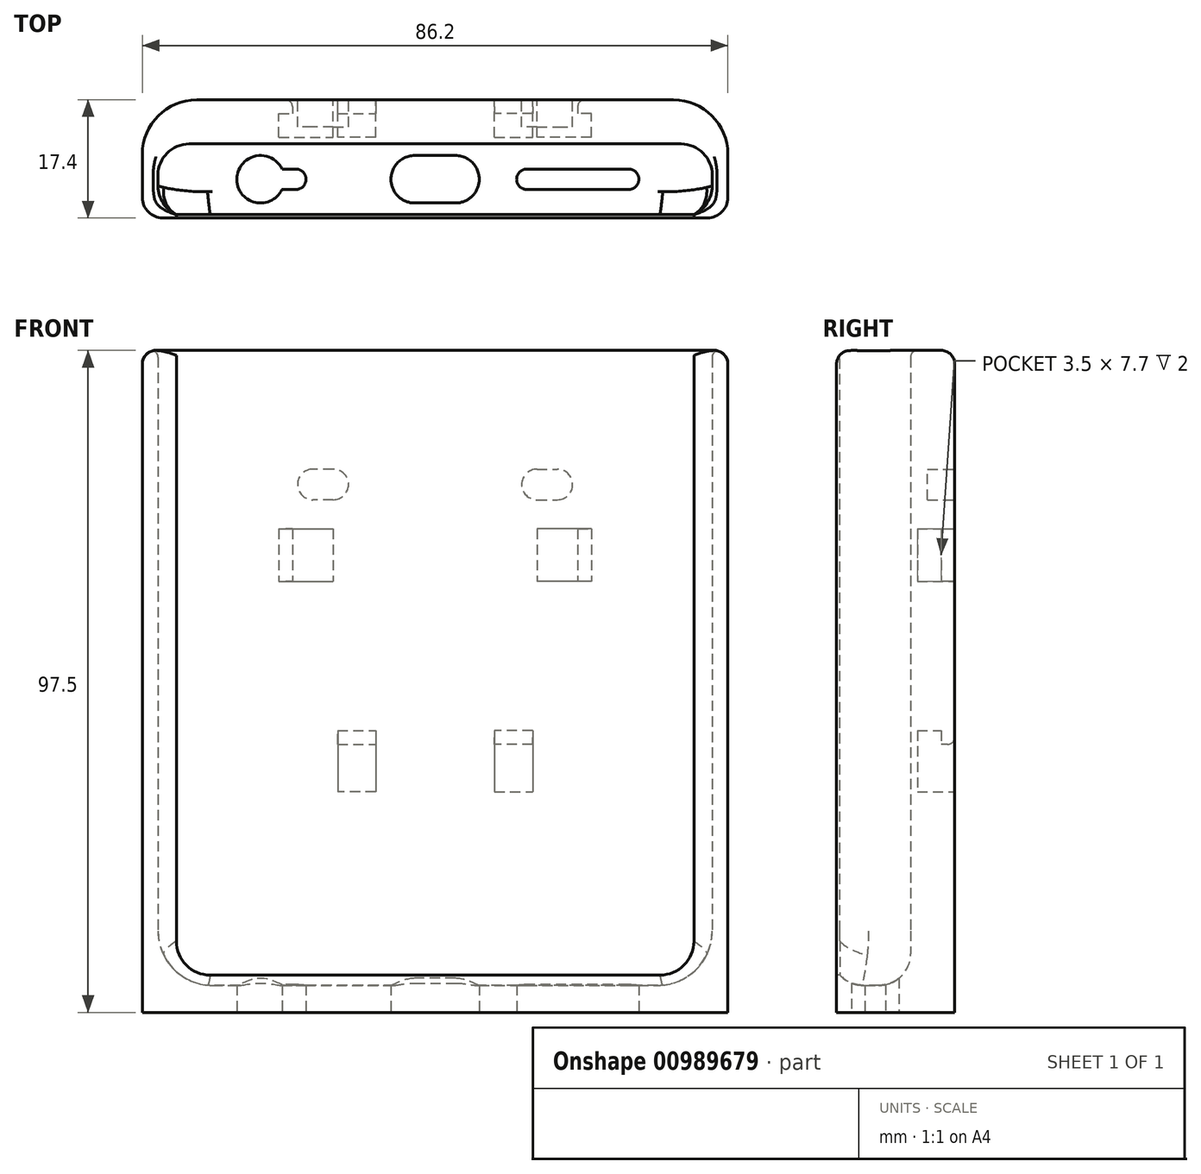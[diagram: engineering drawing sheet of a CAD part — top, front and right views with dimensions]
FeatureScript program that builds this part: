
annotation { "Feature Type Name" : "Feature", "Feature Type Description" : "" }
export const myFeature = defineFeature(function(context is Context, id is Id, definition is map)
    precondition{}
    {
        {
            var Q0;
            Q0=qCreatedBy(makeId("Front.planeOp"),FACE);
            var sketch = newSketch(context, id + "F0", { "sketchPlane" : qUnion([Q0])});
            skLineSegment(sketch, "E0", {"start": v(0, -32.88) * mm, "end": v(0, 44.67) * mm, "construction": true});
            skLineSegment(sketch, "E1.bottom", {"start": v(-23, 39.76) * mm, "end": v(-15, 39.76) * mm});
            skLineSegment(sketch, "E1.top", {"start": v(-23, 32.06) * mm, "end": v(-15, 32.06) * mm});
            skLineSegment(sketch, "E1.left", {"start": v(-23, 39.76) * mm, "end": v(-23, 32.06) * mm});
            skLineSegment(sketch, "E1.right", {"start": v(-15, 39.76) * mm, "end": v(-15, 32.06) * mm});
            skLineSegment(sketch, "E2.bottom", {"start": v(-8.75, 10.06) * mm, "end": v(-14.35, 10.06) * mm});
            skLineSegment(sketch, "E2.top", {"start": v(-8.75, 1.06) * mm, "end": v(-14.35, 1.06) * mm});
            skLineSegment(sketch, "E2.left", {"start": v(-8.75, 10.06) * mm, "end": v(-8.75, 1.06) * mm});
            skLineSegment(sketch, "E2.right", {"start": v(-14.35, 10.06) * mm, "end": v(-14.35, 1.06) * mm});
            skLineSegment(sketch, "E3.MirrorCS", {"start": v(15, 39.76) * mm, "end": v(15, 32.06) * mm});
            skLineSegment(sketch, "E4.MirrorCS", {"start": v(23, 32.06) * mm, "end": v(15, 32.06) * mm});
            skLineSegment(sketch, "E5.MirrorCS", {"start": v(23, 39.76) * mm, "end": v(23, 32.06) * mm});
            skLineSegment(sketch, "E6.MirrorCS", {"start": v(23, 39.76) * mm, "end": v(15, 39.76) * mm});
            skLineSegment(sketch, "E7.MirrorCS", {"start": v(8.75, 10.06) * mm, "end": v(14.35, 10.06) * mm});
            skLineSegment(sketch, "E8.MirrorCS", {"start": v(8.75, 10.06) * mm, "end": v(8.75, 1.06) * mm});
            skLineSegment(sketch, "E9.MirrorCS", {"start": v(8.75, 1.06) * mm, "end": v(14.35, 1.06) * mm});
            skLineSegment(sketch, "E10.MirrorCS", {"start": v(14.35, 10.06) * mm, "end": v(14.35, 1.06) * mm});
            skSolve(sketch);
        }
        {
            var Q0;
            Q0=qCreatedBy(makeId("Front.planeOp"),FACE);
            var sketch = newSketch(context, id + "F1", { "sketchPlane" : qUnion([Q0])});
            skLineSegment(sketch, "E11", {"start": v(0, -37.74) * mm, "end": v(0, 51.46) * mm, "construction": true});
            skLineSegment(sketch, "E12.bottom", {"start": v(0, 66.06) * mm, "end": v(-40.6, 66.06) * mm});
            skLineSegment(sketch, "E12.top", {"start": v(0, -28.94) * mm, "end": v(-32.6, -28.94) * mm});
            skLineSegment(sketch, "E12.left", {"start": v(0, 66.06) * mm, "end": v(0, -28.94) * mm});
            skLineSegment(sketch, "E12.right", {"start": v(-40.6, 66.06) * mm, "end": v(-40.6, -20.94) * mm});
            skPoint(sketch, "E13.visualSharp", {"position": v(-40.6, -28.94) * mm});
            skArc(sketch, "E13.filletArc", {"start": v(-40.6, -20.94) * mm, "mid": v(-38.26, -26.6) * mm, "end": v(-32.6, -28.94) * mm});
            skSolve(sketch);
        }
        {
            var Q0;
            Q0=qCreatedBy(makeId("Front.planeOp"),FACE);
            var sketch = newSketch(context, id + "F2", { "sketchPlane" : qUnion([Q0])});
            skLineSegment(sketch, "E14.bottom", {"start": v(0, 66.06) * mm, "end": v(-43.1, 66.06) * mm});
            skLineSegment(sketch, "E14.top", {"start": v(0, -31.44) * mm, "end": v(-43.1, -31.44) * mm});
            skLineSegment(sketch, "E14.right", {"start": v(-43.1, 66.06) * mm, "end": v(-43.1, -31.44) * mm});
            skPoint(sketch, "E15.visualSharp", {"position": v(-43.1, -31.44) * mm});
            skLineSegment(sketch, "E15.filletArc", {"start": v(-43.1, -31.44) * mm, "end": v(-43.1, -31.44) * mm});
            skLineSegment(sketch, "E16.MirrorCS", {"start": v(0, 66.06) * mm, "end": v(43.1, 66.06) * mm});
            skLineSegment(sketch, "E17.MirrorCS", {"start": v(43.1, 66.06) * mm, "end": v(43.1, -31.44) * mm});
            skLineSegment(sketch, "E18.MirrorCS", {"start": v(43.1, -31.44) * mm, "end": v(43.1, -31.44) * mm});
            skLineSegment(sketch, "E19.MirrorCS", {"start": v(0, -31.44) * mm, "end": v(43.1, -31.44) * mm});
            skSolve(sketch);
        }
        {
            var Q0;
            Q0=qSketchRegion(id+"F2",true);
            extrude(context, id + "F3", {"entities" : qUnion([Q0]), "depth" : 17.4 * mm, "offsetDistance" : 25 * mm});
        }
        {
            var Q0;
            Q0=qSketchRegion(id+"F0",true);
            extrude(context, id + "F4", {"entities" : qUnion([Q0]), "operationType" : NewBodyOperationType.REMOVE, "depth" : 5.5 * mm, "offsetDistance" : 25 * mm});
        }
        {
            var Q0;
            Q0=qCreatedBy(makeId("Front.planeOp"),FACE);
            cPlane(context, id + "F5", {"entities" : qUnion([Q0]), "cplaneType" : CPlaneType.OFFSET, "offset" : 6.5 * mm, "width" : 150 * mm, "height" : 150 * mm});
        }
        {
            var Q0;
            Q0=qCreatedBy(id+"F5.planeOp",FACE);
            var sketch = newSketch(context, id + "F6", { "sketchPlane" : qUnion([Q0])});
            skLineSegment(sketch, "E20", {"start": v(0, -47.03) * mm, "end": v(0, 63.52) * mm, "construction": true});
            skLineSegment(sketch, "E21.right", {"start": v(0, 66.06) * mm, "end": v(0, 51.73) * mm, "construction": true});
            skLineSegment(sketch, "E22.bottom", {"start": v(-40.8, 66.06) * mm, "end": v(0, 66.06) * mm});
            skLineSegment(sketch, "E22.top", {"start": v(-32.8, -27.44) * mm, "end": v(0, -27.44) * mm});
            skLineSegment(sketch, "E22.left", {"start": v(-40.8, 66.06) * mm, "end": v(-40.8, -19.44) * mm});
            skLineSegment(sketch, "E22.right", {"start": v(0, 66.06) * mm, "end": v(0, -27.44) * mm});
            skPoint(sketch, "E23.visualSharp", {"position": v(-40.8, -27.44) * mm});
            skArc(sketch, "E23.filletArc", {"start": v(-40.8, -19.44) * mm, "mid": v(-38.46, -25.1) * mm, "end": v(-32.8, -27.44) * mm});
            skLineSegment(sketch, "E24.MirrorCS", {"start": v(32.8, -27.44) * mm, "end": v(0, -27.44) * mm});
            skArc(sketch, "E25.MirrorCS", {"start": v(40.8, -19.44) * mm, "mid": v(38.46, -25.1) * mm, "end": v(32.8, -27.44) * mm});
            skLineSegment(sketch, "E26.MirrorCS", {"start": v(40.8, 66.06) * mm, "end": v(40.8, -19.44) * mm});
            skLineSegment(sketch, "E27.MirrorCS", {"start": v(40.8, 66.06) * mm, "end": v(0, 66.06) * mm});
            skSolve(sketch);
        }
        {
            var Q0;
            Q0=qSketchRegion(id+"F6",true);
            extrude(context, id + "F7", {"entities" : qUnion([Q0]), "operationType" : NewBodyOperationType.REMOVE, "depth" : 10.4 * mm, "offsetDistance" : 25 * mm});
        }
        {
            var Q0;
            Q0=makeQuery(id+"F3.opExtrude","CAP_FACE",FACE,{"disambiguationData":[OSD([sQuery(id+"F2.wireOp",EDGE,"E14.bottom"),sQuery(id+"F2.wireOp",EDGE,"E14.top"),sQuery(id+"F2.wireOp",EDGE,"E14.right"),sQuery(id+"F2.wireOp",EDGE,"E15.filletArc"),sQuery(id+"F2.wireOp",EDGE,"E16.MirrorCS"),sQuery(id+"F2.wireOp",EDGE,"E17.MirrorCS"),sQuery(id+"F2.wireOp",EDGE,"E18.MirrorCS"),sQuery(id+"F2.wireOp",EDGE,"E19.MirrorCS")])],"isStart":false});
            var sketch = newSketch(context, id + "F8", { "sketchPlane" : qUnion([Q0])});
            skLineSegment(sketch, "E28", {"start": v(0, 66.06) * mm, "end": v(0, 61.95) * mm, "construction": true});
            skLineSegment(sketch, "E29.bottom", {"start": v(-38.1, 66.06) * mm, "end": v(0, 66.06) * mm});
            skLineSegment(sketch, "E29.top", {"start": v(-33.1, -25.94) * mm, "end": v(0, -25.94) * mm});
            skLineSegment(sketch, "E29.left", {"start": v(-38.1, 66.06) * mm, "end": v(-38.1, -20.94) * mm});
            skPoint(sketch, "E30.visualSharp", {"position": v(-38.1, -25.94) * mm});
            skArc(sketch, "E30.filletArc", {"start": v(-38.1, -20.94) * mm, "mid": v(-36.64, -24.48) * mm, "end": v(-33.1, -25.94) * mm});
            skLineSegment(sketch, "E31.trimOffspring", {"start": v(0, -25.94) * mm, "end": v(0, -47.05) * mm, "construction": true});
            skLineSegment(sketch, "E32.MirrorCS", {"start": v(33.1, -25.94) * mm, "end": v(0, -25.94) * mm});
            skArc(sketch, "E33.MirrorCS", {"start": v(38.1, -20.94) * mm, "mid": v(36.64, -24.48) * mm, "end": v(33.1, -25.94) * mm});
            skLineSegment(sketch, "E34.MirrorCS", {"start": v(38.1, 66.06) * mm, "end": v(38.1, -20.94) * mm});
            skLineSegment(sketch, "E35.MirrorCS", {"start": v(38.1, 66.06) * mm, "end": v(0, 66.06) * mm});
            skSolve(sketch);
        }
        {
            var Q0;
            Q0=qSketchRegion(id+"F8",true);
            extrude(context, id + "F9", {"entities" : qUnion([Q0]), "operationType" : NewBodyOperationType.REMOVE, "endBound" : BoundingType.UP_TO_NEXT, "oppositeDirection" : true, "depth" : 25 * mm, "offsetDistance" : 25 * mm});
        }
        {
            var Q0;
            Q0=makeQuery(id+"F7.boolean.opBoolean","COPY",EDGE,{"derivedFrom":makeQuery(id+"F7.opExtrude","CAP_EDGE",EDGE,{"disambiguationData":[OSD([sQuery(id+"F6.wireOp",EDGE,"E22.left")])],"isStart":true})});
            fillet(context, id + "F10", {"entities" : qUnion([Q0]), "radius" : 4.6 * mm, "tangentPropagation" : true, "allowEdgeOverflow" : false});
        }
        {
            var Q0;
            Q0=makeQuery(id+"F7.boolean.opBoolean","COPY",EDGE,{"derivedFrom":makeQuery(id+"F7.opExtrude","CAP_EDGE",EDGE,{"disambiguationData":[OSD([sQuery(id+"F6.wireOp",EDGE,"E22.left")])],"isStart":false})});
            fillet(context, id + "F11", {"entities" : qUnion([Q0]), "radius" : 4.6 * mm, "tangentPropagation" : true, "allowEdgeOverflow" : false});
        }
        {
            var Q0;
            Q0=makeQuery(id+"F11.opFillet","BLEND_EDGE",EDGE,{"blendedFrom":[makeQuery(id+"F7.boolean.opBoolean","COPY",EDGE,{"derivedFrom":makeQuery(id+"F7.opExtrude","CAP_EDGE",EDGE,{"disambiguationData":[OSD([sQuery(id+"F6.wireOp",EDGE,"E26.MirrorCS")])],"isStart":false})}),makeQuery(id+"F3.opExtrude","SWEPT_FACE",FACE,{"disambiguationData":[OSD([sQuery(id+"F2.wireOp",EDGE,"E14.bottom"),sQuery(id+"F2.wireOp",EDGE,"E16.MirrorCS")])]})],"blendedInto":[makeQuery(id+"F3.opExtrude","SWEPT_FACE",FACE,{"disambiguationData":[OSD([sQuery(id+"F2.wireOp",EDGE,"E14.bottom"),sQuery(id+"F2.wireOp",EDGE,"E16.MirrorCS")])]})]});
            var Q1;
            {var subQ0=sQuery(id+"F6.wireOp",EDGE,"E27.MirrorCS");var subQ1=sQuery(id+"F6.wireOp",EDGE,"E26.MirrorCS");var subQ2=sQuery(id+"F6.wireOp",EDGE,"E22.bottom");Q1=makeQuery(id+"F9.boolean.opBoolean","SPLIT",EDGE,{"disambiguationData":[TD([makeQuery(id+"F7.boolean.opBoolean","COPY",FACE,{"derivedFrom":makeQuery(id+"F7.opExtrude","SWEPT_FACE",FACE,{"disambiguationData":[OSD([subQ1])]})})])],"derivedFrom":makeQuery(id+"F7.boolean.opBoolean","COPY",EDGE,{"derivedFrom":makeQuery(id+"F7.opExtrude","CAP_EDGE",EDGE,{"disambiguationData":[OSD([subQ2,subQ0])],"isStart":false})})});}
            fillet(context, id + "F12", {"entities" : qUnion([Q0, Q1]), "radius" : 1 * mm, "tangentPropagation" : true, "allowEdgeOverflow" : false});
        }
        {
            var Q0;
            Q0=makeQuery(id+"F4.boolean.opBoolean","COPY",FACE,{"derivedFrom":makeQuery(id+"F4.opExtrude","SWEPT_FACE",FACE,{"disambiguationData":[OSD([sQuery(id+"F0.wireOp",EDGE,"E4.MirrorCS")])]})});
            var sketch = newSketch(context, id + "F13", { "sketchPlane" : qUnion([Q0])});
            skLineSegment(sketch, "E36.bottom", {"start": v(23, 0) * mm, "end": v(22, 0) * mm});
            skLineSegment(sketch, "E36.top", {"start": v(23, -2) * mm, "end": v(21, -2) * mm});
            skLineSegment(sketch, "E36.left", {"start": v(23, 0) * mm, "end": v(23, -2) * mm});
            skLineSegment(sketch, "E36.right", {"start": v(21, -1) * mm, "end": v(21, -2) * mm});
            skPoint(sketch, "E37.visualSharp", {"position": v(21, 0) * mm});
            skArc(sketch, "E37.filletArc", {"start": v(22, 0) * mm, "mid": v(21.3, -0.3) * mm, "end": v(21, -1) * mm});
            skSolve(sketch);
        }
        {
            var Q0;
            Q0=qSketchRegion(id+"F13",true);
            extrude(context, id + "F14", {"entities" : qUnion([Q0]), "operationType" : NewBodyOperationType.ADD, "endBound" : BoundingType.UP_TO_NEXT, "depth" : 25 * mm, "offsetDistance" : 25 * mm});
        }
        {
            var Q0;
            Q0=makeQuery(id+"F4.boolean.opBoolean","COPY",FACE,{"derivedFrom":makeQuery(id+"F4.opExtrude","SWEPT_FACE",FACE,{"disambiguationData":[OSD([sQuery(id+"F0.wireOp",EDGE,"E1.top")])]})});
            var sketch = newSketch(context, id + "F15", { "sketchPlane" : qUnion([Q0])});
            skLineSegment(sketch, "E38.bottom", {"start": v(-23, 0) * mm, "end": v(-22, 0) * mm});
            skLineSegment(sketch, "E38.top", {"start": v(-23, -2) * mm, "end": v(-21, -2) * mm});
            skLineSegment(sketch, "E38.left", {"start": v(-23, 0) * mm, "end": v(-23, -2) * mm});
            skLineSegment(sketch, "E38.right", {"start": v(-21, -1) * mm, "end": v(-21, -2) * mm});
            skPoint(sketch, "E39.visualSharp", {"position": v(-21, 0) * mm});
            skArc(sketch, "E39.filletArc", {"start": v(-21, -1) * mm, "mid": v(-21.3, -0.3) * mm, "end": v(-22, 0) * mm});
            skSolve(sketch);
        }
        {
            var Q0;
            Q0=qSketchRegion(id+"F15",true);
            extrude(context, id + "F16", {"entities" : qUnion([Q0]), "operationType" : NewBodyOperationType.ADD, "endBound" : BoundingType.UP_TO_NEXT, "depth" : 25 * mm, "offsetDistance" : 25 * mm});
        }
        {
            var Q0;
            Q0=makeQuery(id+"F4.boolean.opBoolean","COPY",FACE,{"derivedFrom":makeQuery(id+"F4.opExtrude","SWEPT_FACE",FACE,{"disambiguationData":[OSD([sQuery(id+"F0.wireOp",EDGE,"E2.left")])]})});
            var sketch = newSketch(context, id + "F17", { "sketchPlane" : qUnion([Q0])});
            skLineSegment(sketch, "E40.bottom", {"start": v(0, 10.06) * mm, "end": v(2, 10.06) * mm});
            skLineSegment(sketch, "E40.top", {"start": v(1, 8.06) * mm, "end": v(2, 8.06) * mm});
            skLineSegment(sketch, "E40.left", {"start": v(0, 10.06) * mm, "end": v(0, 9.06) * mm});
            skLineSegment(sketch, "E40.right", {"start": v(2, 10.06) * mm, "end": v(2, 8.06) * mm});
            skPoint(sketch, "E41.visualSharp", {"position": v(0, 8.06) * mm});
            skArc(sketch, "E41.filletArc", {"start": v(0, 9.06) * mm, "mid": v(0.3, 8.35) * mm, "end": v(1, 8.06) * mm});
            skSolve(sketch);
        }
        {
            var Q0;
            Q0=qSketchRegion(id+"F17",true);
            extrude(context, id + "F18", {"entities" : qUnion([Q0]), "operationType" : NewBodyOperationType.ADD, "endBound" : BoundingType.UP_TO_NEXT, "depth" : 25 * mm, "offsetDistance" : 25 * mm});
        }
        {
            var Q0;
            Q0=makeQuery(id+"F4.boolean.opBoolean","COPY",FACE,{"derivedFrom":makeQuery(id+"F4.opExtrude","SWEPT_FACE",FACE,{"disambiguationData":[OSD([sQuery(id+"F0.wireOp",EDGE,"E8.MirrorCS")])]})});
            var sketch = newSketch(context, id + "F19", { "sketchPlane" : qUnion([Q0])});
            skLineSegment(sketch, "E42.bottom", {"start": v(0, 10.06) * mm, "end": v(-2, 10.06) * mm});
            skLineSegment(sketch, "E42.top", {"start": v(-1, 8.06) * mm, "end": v(-2, 8.06) * mm});
            skLineSegment(sketch, "E42.left", {"start": v(0, 10.06) * mm, "end": v(0, 9.06) * mm});
            skLineSegment(sketch, "E42.right", {"start": v(-2, 10.06) * mm, "end": v(-2, 8.06) * mm});
            skPoint(sketch, "E43.visualSharp", {"position": v(0, 8.06) * mm});
            skArc(sketch, "E43.filletArc", {"start": v(-1, 8.06) * mm, "mid": v(-0.3, 8.35) * mm, "end": v(0, 9.06) * mm});
            skSolve(sketch);
        }
        {
            var Q0;
            Q0=qSketchRegion(id+"F19",true);
            extrude(context, id + "F20", {"entities" : qUnion([Q0]), "operationType" : NewBodyOperationType.ADD, "endBound" : BoundingType.UP_TO_NEXT, "depth" : 25 * mm, "offsetDistance" : 25 * mm});
        }
        {
            var Q0;
            Q0=makeQuery(id+"F3.opExtrude","SWEPT_FACE",FACE,{"disambiguationData":[OSD([sQuery(id+"F2.wireOp",EDGE,"E14.top"),sQuery(id+"F2.wireOp",EDGE,"E19.MirrorCS")])]});
            var sketch = newSketch(context, id + "F21", { "sketchPlane" : qUnion([Q0])});
            skLineSegment(sketch, "E44", {"start": v(-40.57, 11.7) * mm, "end": v(-17, 11.7) * mm, "construction": true});
            skLineSegment(sketch, "E45", {"start": v(0, 24.83) * mm, "end": v(0, 15.2) * mm, "construction": true});
            skLineSegment(sketch, "E46.bottom", {"start": v(-3, 15.2) * mm, "end": v(0, 15.2) * mm});
            skLineSegment(sketch, "E46.left", {"start": v(-6.5, 11.7) * mm, "end": v(-6.5, 11.7) * mm});
            skLineSegment(sketch, "E47.trimOffspring", {"start": v(0, 8.91) * mm, "end": v(0, -15.6) * mm, "construction": true});
            skPoint(sketch, "E48.visualSharp", {"position": v(-6.5, 15.2) * mm});
            skArc(sketch, "E48.filletArc", {"start": v(-3, 15.2) * mm, "mid": v(-5.47, 14.17) * mm, "end": v(-6.5, 11.7) * mm});
            skArc(sketch, "E49.MirrorCS", {"start": v(-3, 8.2) * mm, "mid": v(-5.47, 9.23) * mm, "end": v(-6.5, 11.7) * mm});
            skLineSegment(sketch, "E50.MirrorCS", {"start": v(-3, 8.2) * mm, "end": v(0, 8.2) * mm});
            skLineSegment(sketch, "E51.MirrorCS", {"start": v(3, 15.2) * mm, "end": v(0, 15.2) * mm});
            skArc(sketch, "E52.MirrorCS", {"start": v(3, 15.2) * mm, "mid": v(5.47, 14.17) * mm, "end": v(6.5, 11.7) * mm});
            skArc(sketch, "E53.MirrorCS", {"start": v(3, 8.2) * mm, "mid": v(5.47, 9.23) * mm, "end": v(6.5, 11.7) * mm});
            skLineSegment(sketch, "E54.MirrorCS", {"start": v(3, 8.2) * mm, "end": v(0, 8.2) * mm});
            skLineSegment(sketch, "E55.trimOffspring", {"start": v(-17, 11.7) * mm, "end": v(38.86, 11.7) * mm, "construction": true});
            skArc(sketch, "E56.0.startCap", {"start": v(13.5, 10.2) * mm, "mid": v(12, 11.7) * mm, "end": v(13.5, 13.2) * mm});
            skArc(sketch, "E56.0.endCap", {"start": v(28.5, 13.2) * mm, "mid": v(30, 11.7) * mm, "end": v(28.5, 10.2) * mm});
            skLineSegment(sketch, "E56.0.left", {"start": v(13.5, 13.2) * mm, "end": v(28.5, 13.2) * mm});
            skLineSegment(sketch, "E56.0.right", {"start": v(13.5, 10.2) * mm, "end": v(28.5, 10.2) * mm});
            skArc(sketch, "E57.0.endCap", {"start": v(-20.5, 13.2) * mm, "mid": v(-19, 11.7) * mm, "end": v(-20.5, 10.2) * mm});
            skLineSegment(sketch, "E57.0.left", {"start": v(-22.54, 13.2) * mm, "end": v(-20.5, 13.2) * mm});
            skLineSegment(sketch, "E57.0.right", {"start": v(-22.54, 10.2) * mm, "end": v(-20.5, 10.2) * mm});
            skArc(sketch, "E58", {"start": v(-22.54, 13.2) * mm, "mid": v(-29.2, 11.7) * mm, "end": v(-22.54, 10.2) * mm});
            skSolve(sketch);
        }
        {
            var Q0;
            Q0=qSketchRegion(id+"F21",true);
            extrude(context, id + "F22", {"entities" : qUnion([Q0]), "operationType" : NewBodyOperationType.REMOVE, "endBound" : BoundingType.UP_TO_NEXT, "oppositeDirection" : true, "depth" : 25 * mm, "offsetDistance" : 25 * mm});
        }
        {
            var Q0;
            Q0=makeQuery(id+"F3.opExtrude","CAP_EDGE",EDGE,{"disambiguationData":[OSD([sQuery(id+"F2.wireOp",EDGE,"E14.right")])],"isStart":true});
            var Q1;
            Q1=makeQuery(id+"F3.opExtrude","CAP_EDGE",EDGE,{"disambiguationData":[OSD([sQuery(id+"F2.wireOp",EDGE,"E17.MirrorCS")])],"isStart":true});
            fillet(context, id + "F23", {"entities" : qUnion([Q0, Q1]), "radius" : 8 * mm, "tangentPropagation" : true, "allowEdgeOverflow" : false});
        }
        {
            var Q0;
            Q0=makeQuery(id+"F3.opExtrude","CAP_EDGE",EDGE,{"disambiguationData":[OSD([sQuery(id+"F2.wireOp",EDGE,"E14.right")])],"isStart":false});
            var Q1;
            Q1=makeQuery(id+"F3.opExtrude","CAP_EDGE",EDGE,{"disambiguationData":[OSD([sQuery(id+"F2.wireOp",EDGE,"E17.MirrorCS")])],"isStart":false});
            fillet(context, id + "F24", {"entities" : qUnion([Q0, Q1]), "radius" : 3 * mm, "tangentPropagation" : true, "allowEdgeOverflow" : false});
        }
        {
            var Q0;
            Q0=makeQuery(id+"F24.opFillet","BLEND_EDGE",EDGE,{"blendedFrom":[makeQuery(id+"F3.opExtrude","CAP_EDGE",EDGE,{"disambiguationData":[OSD([sQuery(id+"F2.wireOp",EDGE,"E14.right")])],"isStart":false}),makeQuery(id+"F3.opExtrude","SWEPT_FACE",FACE,{"disambiguationData":[OSD([sQuery(id+"F2.wireOp",EDGE,"E14.bottom"),sQuery(id+"F2.wireOp",EDGE,"E16.MirrorCS")])]})],"blendedInto":[makeQuery(id+"F3.opExtrude","SWEPT_FACE",FACE,{"disambiguationData":[OSD([sQuery(id+"F2.wireOp",EDGE,"E14.bottom"),sQuery(id+"F2.wireOp",EDGE,"E16.MirrorCS")])]})]});
            fillet(context, id + "F25", {"entities" : qUnion([Q0]), "radius" : 2 * mm, "tangentPropagation" : true, "allowEdgeOverflow" : false});
        }
        {
            var Q0;
            Q0=makeQuery(id+"F20.boolean.opBoolean","MERGE",FACE,{"derivedFrom":[makeQuery(id+"F18.boolean.opBoolean","MERGE",FACE,{"derivedFrom":[makeQuery(id+"F16.boolean.opBoolean","MERGE",FACE,{"derivedFrom":[makeQuery(id+"F14.boolean.opBoolean","MERGE",FACE,{"derivedFrom":[makeQuery(id+"F3.opExtrude","CAP_FACE",FACE,{"disambiguationData":[OSD([sQuery(id+"F2.wireOp",EDGE,"E14.bottom"),sQuery(id+"F2.wireOp",EDGE,"E14.top"),sQuery(id+"F2.wireOp",EDGE,"E14.right"),sQuery(id+"F2.wireOp",EDGE,"E16.MirrorCS"),sQuery(id+"F2.wireOp",EDGE,"E17.MirrorCS"),sQuery(id+"F2.wireOp",EDGE,"E19.MirrorCS")])],"isStart":true}),makeQuery(id+"F14.opExtrude","SWEPT_FACE",FACE,{"disambiguationData":[OSD([sQuery(id+"F13.wireOp",EDGE,"E36.bottom")])]})]}),makeQuery(id+"F16.opExtrude","SWEPT_FACE",FACE,{"disambiguationData":[OSD([sQuery(id+"F15.wireOp",EDGE,"E38.bottom")])]})]}),makeQuery(id+"F18.opExtrude","SWEPT_FACE",FACE,{"disambiguationData":[OSD([sQuery(id+"F17.wireOp",EDGE,"E40.left")])]})]}),makeQuery(id+"F20.opExtrude","SWEPT_FACE",FACE,{"disambiguationData":[OSD([sQuery(id+"F19.wireOp",EDGE,"E42.left")])]})]});
            var sketch = newSketch(context, id + "F26", { "sketchPlane" : qUnion([Q0])});
            skLineSegment(sketch, "E59", {"start": v(0, 68.54) * mm, "end": v(0, -55.98) * mm, "construction": true});
            skArc(sketch, "E60", {"start": v(15, 48.56) * mm, "mid": v(12.75, 46.3) * mm, "end": v(15, 44.06) * mm});
            skArc(sketch, "E61", {"start": v(18, 44.06) * mm, "mid": v(20.25, 46.3) * mm, "end": v(18, 48.56) * mm});
            skLineSegment(sketch, "E62", {"start": v(15, 48.56) * mm, "end": v(18, 48.56) * mm});
            skLineSegment(sketch, "E63", {"start": v(15, 44.06) * mm, "end": v(18, 44.06) * mm});
            skArc(sketch, "E64.MirrorCS", {"start": v(-15, 48.56) * mm, "mid": v(-12.75, 46.3) * mm, "end": v(-15, 44.06) * mm});
            skLineSegment(sketch, "E65.MirrorCS", {"start": v(-15, 48.56) * mm, "end": v(-18, 48.56) * mm});
            skLineSegment(sketch, "E66.MirrorCS", {"start": v(-15, 44.06) * mm, "end": v(-18, 44.06) * mm});
            skArc(sketch, "E67.MirrorCS", {"start": v(-18, 44.06) * mm, "mid": v(-20.25, 46.3) * mm, "end": v(-18, 48.56) * mm});
            skSolve(sketch);
        }
        {
            var Q0;
            Q0=qSketchRegion(id+"F26",true);
            extrude(context, id + "F27", {"entities" : qUnion([Q0]), "operationType" : NewBodyOperationType.REMOVE, "oppositeDirection" : true, "depth" : 4 * mm, "offsetDistance" : 25 * mm});
        }
    });
